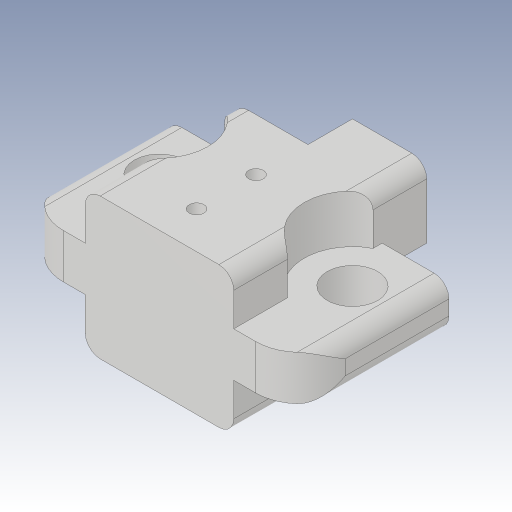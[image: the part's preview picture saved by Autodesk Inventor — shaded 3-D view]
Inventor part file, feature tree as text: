
AUTODESK INVENTOR PART (.ipt)
format: ipt  version: 2023.3 (Build 273359000, 359)  size: 331,264 bytes
history: native  units: in
note: dims shown in document units (in); Inventor stores cm internally (conversion verified against a paired STEP export)
features: sketch x9, hole x6, projected_geometry x6, extrude x4, fillet x1
ambient origin geometry x8: Origin, YZ Plane, XZ Plane, XY Plane, X Axis, Y Axis, Z Axis, Center Point
bodies: Body1 (feature_tree)
feature tree (26):
  sketch  "Skizze3"  dims[d9=0.3937in d10=0.0in d12=0.3937in]
  extrude  "Extrusion3"  Depth=0.3937in
  extrude  "Extrusion4"  Depth=0.0394in
  fillet  "Rundung1"  Radius=0.3937in
  sketch  "Skizze5"  dims[d13=0.374in d14=0.0394in d17=0.3937in d18=0.0in]
  hole  "Bohrung3"  [1 undecoded]
  sketch  "Skizze6"  dims[d19=0.1181in]
  hole  "Bohrung5"  [1 undecoded]
  sketch  "Skizze9"  dims[d42=0.1181in d43=0.0in]
  hole  "Bohrung6"  [1 undecoded]
  hole  "Bohrung7"  [1 undecoded]
  hole  "Bohrung8"  [1 undecoded]
  extrude  "Extrusion7"  Depth=0.0394in
  hole  "Bohrung9"  [1 undecoded]
  extrude  "Extrusion8"  TaperAngle=0.0deg  [1 undecoded]
  sketch  "Skizze7"  dims[d34=0.2362in d35=0.2362in d36=0.4331in d37=0.0984in d38=90.0deg d39=0.4724in d40=0.0in d41=0.1181in]
  projected_geometry  "Projizierte Kontur2"
  projected_geometry  "Projizierte Kontur3"
  sketch  "Skizze10"  dims[d52=0.0394in d53=0.2362in d54=0.1575in d55=0.0787in d56=90.0deg d57=0.315in d58=0.0in d83=0.1772in]
  sketch  "Skizze11"  dims[d84=0.1181in]
  projected_geometry  "Projizierte Kontur4"
  projected_geometry  "Projizierte Kontur5"
  projected_geometry  "Projizierte Kontur6"
  sketch  "Skizze12"  dims[d85=0.1339in d86=0.2362in d87=0.2559in d88=0.1339in d89=0.5635in d90=0.4724in d91=0.0in]
  projected_geometry  "Projizierte Kontur7"
  sketch  "Skizze13"  dims[d92=0.1339in d93=0.2362in d94=0.2559in d95=0.1339in d96=90.0deg d97=0.315in d98=0.0in d99=0.1339in d100=0.2362in d101=0.2559in d102=0.1339in d103=90.0deg d104=0.315in d105=0.0in d106=0.1181in d107=0.0in d108=0.1181in d109=0.0in d113=0.0591in d114=0.0394in d115=0.2362in d116=0.1575in d117=0.0787in d118=90.0deg d119=0.315in d120=0.0in d122=0.2165in d123=0.0394in d124=0.0in d125=0.0in d8=0.0197in d11=0.0344in d79=0.0in d80=0.0in d81=0.0in d82=0.0in]
note: 7 required parameter values undecoded (feature->parameter linkage not recoverable at this tier; creation-order binding heuristic only, values carry confidence <= 0.55)
